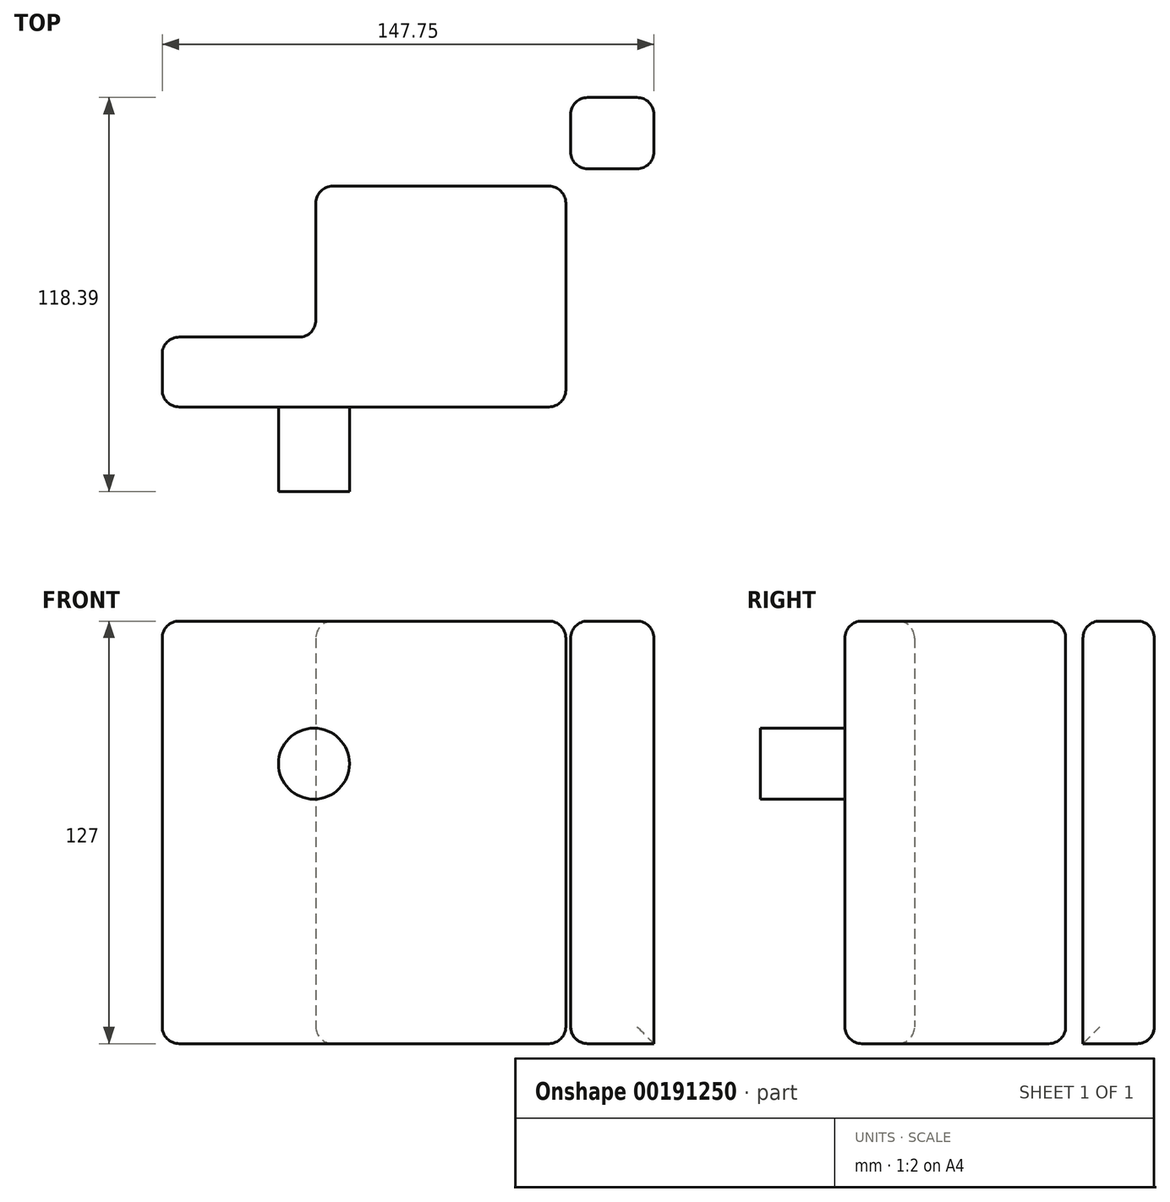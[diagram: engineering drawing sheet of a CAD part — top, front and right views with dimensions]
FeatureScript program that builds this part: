
annotation { "Feature Type Name" : "Feature", "Feature Type Description" : "" }
export const myFeature = defineFeature(function(context is Context, id is Id, definition is map)
    precondition{}
    {
        {
            var Q0;
            Q0=qCreatedBy(makeId("Top.planeOp"),FACE);
            var sketch = newSketch(context, id + "F0", { "sketchPlane" : qUnion([Q0])});
            skLineSegment(sketch, "E0", {"start": v(-63.95, -34.9) * mm, "end": v(57.32, -34.9) * mm});
            skLineSegment(sketch, "E1", {"start": v(57.32, -34.9) * mm, "end": v(57.32, 31.45) * mm});
            skLineSegment(sketch, "E2", {"start": v(57.32, 31.45) * mm, "end": v(-17.78, 31.45) * mm});
            skLineSegment(sketch, "E3", {"start": v(-17.78, 31.45) * mm, "end": v(-17.78, -13.93) * mm});
            skLineSegment(sketch, "E4", {"start": v(-17.78, -13.93) * mm, "end": v(-63.95, -13.93) * mm});
            skLineSegment(sketch, "E5", {"start": v(-63.95, -13.93) * mm, "end": v(-63.95, -34.9) * mm});
            skLineSegment(sketch, "E6.bottom", {"start": v(58.78, 58.09) * mm, "end": v(83.8, 58.09) * mm});
            skLineSegment(sketch, "E6.top", {"start": v(58.78, 36.64) * mm, "end": v(83.8, 36.64) * mm});
            skLineSegment(sketch, "E6.left", {"start": v(58.78, 58.09) * mm, "end": v(58.78, 36.64) * mm});
            skLineSegment(sketch, "E6.right", {"start": v(83.8, 58.09) * mm, "end": v(83.8, 36.64) * mm});
            skLineSegment(sketch, "E7", {"start": v(-17.78, 31.45) * mm, "end": v(58.78, 58.09) * mm});
            skLineSegment(sketch, "E8", {"start": v(58.78, 36.64) * mm, "end": v(57.32, 31.45) * mm});
            skSolve(sketch);
        }
        {
            var Q0;
            Q0=makeQuery(id+"F0.imprint","IMPRINT",FACE,{"disambiguationData":[TD([[makeQuery(id+"F0.imprint","IMPRINT",EDGE,{"derivedFrom":sQuery(id+"F0.wireOp",EDGE,"E6.bottom")}),-1.0]])]});
            var Q1;
            Q1=makeQuery(id+"F0.imprint","IMPRINT",FACE,{"disambiguationData":[TD([[makeQuery(id+"F0.imprint","IMPRINT",EDGE,{"derivedFrom":sQuery(id+"F0.wireOp",EDGE,"E0")}),1.0]])]});
            extrude(context, id + "F1", {"entities" : qUnion([Q0, Q1]), "depth" : 127 * mm});
        }
        {
            var Q0;
            Q0=makeQuery(id+"F1.opExtrude","CAP_FACE",FACE,{"disambiguationData":[OSD([sQuery(id+"F0.wireOp",EDGE,"E0"),sQuery(id+"F0.wireOp",EDGE,"E1"),sQuery(id+"F0.wireOp",EDGE,"E2"),sQuery(id+"F0.wireOp",EDGE,"E3"),sQuery(id+"F0.wireOp",EDGE,"E4"),sQuery(id+"F0.wireOp",EDGE,"E5")])],"isStart":false});
            var Q1;
            Q1=makeQuery(id+"F1.opExtrude","SWEPT_EDGE",EDGE,{"disambiguationData":[OSD([sQuery(id+"F0.wireOp",EDGE,"E0"),sQuery(id+"F0.wireOp",EDGE,"E1")])]});
            var Q2;
            Q2=makeQuery(id+"F1.opExtrude","CAP_EDGE",EDGE,{"disambiguationData":[OSD([sQuery(id+"F0.wireOp",EDGE,"E1")])],"isStart":true});
            var Q3;
            Q3=makeQuery(id+"F1.opExtrude","CAP_EDGE",EDGE,{"disambiguationData":[OSD([sQuery(id+"F0.wireOp",EDGE,"E0")])],"isStart":true});
            var Q4;
            Q4=makeQuery(id+"F1.opExtrude","SWEPT_EDGE",EDGE,{"disambiguationData":[OSD([sQuery(id+"F0.wireOp",EDGE,"E0"),sQuery(id+"F0.wireOp",EDGE,"E5")])]});
            var Q5;
            Q5=makeQuery(id+"F1.opExtrude","SWEPT_EDGE",EDGE,{"disambiguationData":[OSD([sQuery(id+"F0.wireOp",EDGE,"E6.top"),sQuery(id+"F0.wireOp",EDGE,"E6.right")])]});
            var Q6;
            Q6=makeQuery(id+"F1.opExtrude","SWEPT_EDGE",EDGE,{"disambiguationData":[OSD([sQuery(id+"F0.wireOp",EDGE,"E6.bottom"),sQuery(id+"F0.wireOp",EDGE,"E6.right")])]});
            var Q7;
            Q7=makeQuery(id+"F1.opExtrude","SWEPT_EDGE",EDGE,{"disambiguationData":[OSD([sQuery(id+"F0.wireOp",EDGE,"E6.top"),sQuery(id+"F0.wireOp",EDGE,"E6.left"),sQuery(id+"F0.wireOp",EDGE,"E8")])]});
            var Q8;
            Q8=makeQuery(id+"F1.opExtrude","SWEPT_EDGE",EDGE,{"disambiguationData":[OSD([sQuery(id+"F0.wireOp",EDGE,"E6.bottom"),sQuery(id+"F0.wireOp",EDGE,"E6.left"),sQuery(id+"F0.wireOp",EDGE,"E7")])]});
            var Q9;
            Q9=makeQuery(id+"F1.opExtrude","SWEPT_EDGE",EDGE,{"disambiguationData":[OSD([sQuery(id+"F0.wireOp",EDGE,"E1"),sQuery(id+"F0.wireOp",EDGE,"E2"),sQuery(id+"F0.wireOp",EDGE,"E8")])]});
            var Q10;
            Q10=makeQuery(id+"F1.opExtrude","SWEPT_EDGE",EDGE,{"disambiguationData":[OSD([sQuery(id+"F0.wireOp",EDGE,"E2"),sQuery(id+"F0.wireOp",EDGE,"E3"),sQuery(id+"F0.wireOp",EDGE,"E7")])]});
            var Q11;
            Q11=makeQuery(id+"F1.opExtrude","SWEPT_EDGE",EDGE,{"disambiguationData":[OSD([sQuery(id+"F0.wireOp",EDGE,"E3"),sQuery(id+"F0.wireOp",EDGE,"E4")])]});
            var Q12;
            Q12=makeQuery(id+"F1.opExtrude","SWEPT_EDGE",EDGE,{"disambiguationData":[OSD([sQuery(id+"F0.wireOp",EDGE,"E4"),sQuery(id+"F0.wireOp",EDGE,"E5")])]});
            var Q13;
            Q13=makeQuery(id+"F1.opExtrude","CAP_EDGE",EDGE,{"disambiguationData":[OSD([sQuery(id+"F0.wireOp",EDGE,"E4")])],"isStart":true});
            var Q14;
            Q14=makeQuery(id+"F1.opExtrude","CAP_EDGE",EDGE,{"disambiguationData":[OSD([sQuery(id+"F0.wireOp",EDGE,"E3")])],"isStart":true});
            var Q15;
            Q15=makeQuery(id+"F1.opExtrude","CAP_EDGE",EDGE,{"disambiguationData":[OSD([sQuery(id+"F0.wireOp",EDGE,"E2")])],"isStart":true});
            var Q16;
            Q16=makeQuery(id+"F1.opExtrude","CAP_EDGE",EDGE,{"disambiguationData":[OSD([sQuery(id+"F0.wireOp",EDGE,"E6.left")])],"isStart":true});
            var Q17;
            Q17=makeQuery(id+"F1.opExtrude","CAP_EDGE",EDGE,{"disambiguationData":[OSD([sQuery(id+"F0.wireOp",EDGE,"E6.bottom")])],"isStart":true});
            var Q18;
            Q18=makeQuery(id+"F1.opExtrude","CAP_EDGE",EDGE,{"disambiguationData":[OSD([sQuery(id+"F0.wireOp",EDGE,"E5")])],"isStart":true});
            var Q19;
            Q19=makeQuery(id+"F1.opExtrude","CAP_EDGE",EDGE,{"disambiguationData":[OSD([sQuery(id+"F0.wireOp",EDGE,"E6.left")])],"isStart":false});
            var Q20;
            Q20=makeQuery(id+"F1.opExtrude","CAP_EDGE",EDGE,{"disambiguationData":[OSD([sQuery(id+"F0.wireOp",EDGE,"E6.bottom")])],"isStart":false});
            var Q21;
            Q21=makeQuery(id+"F1.opExtrude","CAP_EDGE",EDGE,{"disambiguationData":[OSD([sQuery(id+"F0.wireOp",EDGE,"E6.right")])],"isStart":false});
            var Q22;
            Q22=makeQuery(id+"F1.opExtrude","CAP_EDGE",EDGE,{"disambiguationData":[OSD([sQuery(id+"F0.wireOp",EDGE,"E6.top")])],"isStart":false});
            fillet(context, id + "F2", {"entities" : qUnion([Q0, Q1, Q2, Q3, Q4, Q5, Q6, Q7, Q8, Q9, Q10, Q11, Q12, Q13, Q14, Q15, Q16, Q17, Q18, Q19, Q20, Q21, Q22]), "radius" : 5.08 * mm, "tangentPropagation" : true, "allowEdgeOverflow" : false});
        }
        {
            var Q0;
            Q0=makeQuery(id+"F1.opExtrude","SWEPT_FACE",FACE,{"disambiguationData":[OSD([sQuery(id+"F0.wireOp",EDGE,"E0")])]});
            var sketch = newSketch(context, id + "F3", { "sketchPlane" : qUnion([Q0])});
            skCircle(sketch, "E9", {"center": v(-18.36, 84.15) * mm, "radius": 10.67 * mm});
            skSolve(sketch);
        }
        {
            var Q0;
            Q0 = qSketchRegion(id + "F3", true);
            extrude(context, id + "F4", {"entities" : qUnion([Q0]), "operationType" : NewBodyOperationType.ADD, "depth" : 25.4 * mm});
        }
    });
